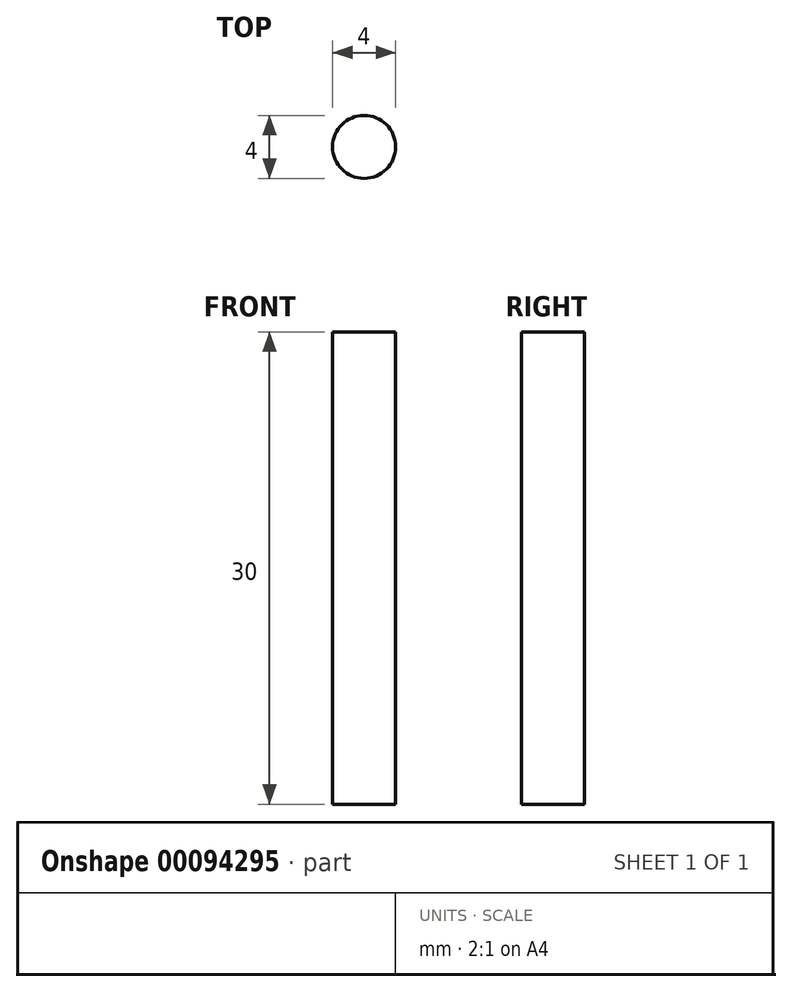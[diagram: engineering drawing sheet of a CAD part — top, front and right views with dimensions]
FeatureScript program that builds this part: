
annotation { "Feature Type Name" : "Feature", "Feature Type Description" : "" }
export const myFeature = defineFeature(function(context is Context, id is Id, definition is map)
    precondition{}
    {
        {
            var Q0;
            Q0=qCreatedBy(makeId("Top.planeOp"),FACE);
            var sketch = newSketch(context, id + "F0", { "sketchPlane" : qUnion([Q0])});
            skCircle(sketch, "E0", {"center": v(0, 0) * mm, "radius": 2 * mm});
            skSolve(sketch);
        }
        {
            var Q0;
            Q0 = qSketchRegion(id + "F0", true);
            extrude(context, id + "F1", {"entities" : qUnion([Q0]), "depth" : 30 * mm});
        }
    });
